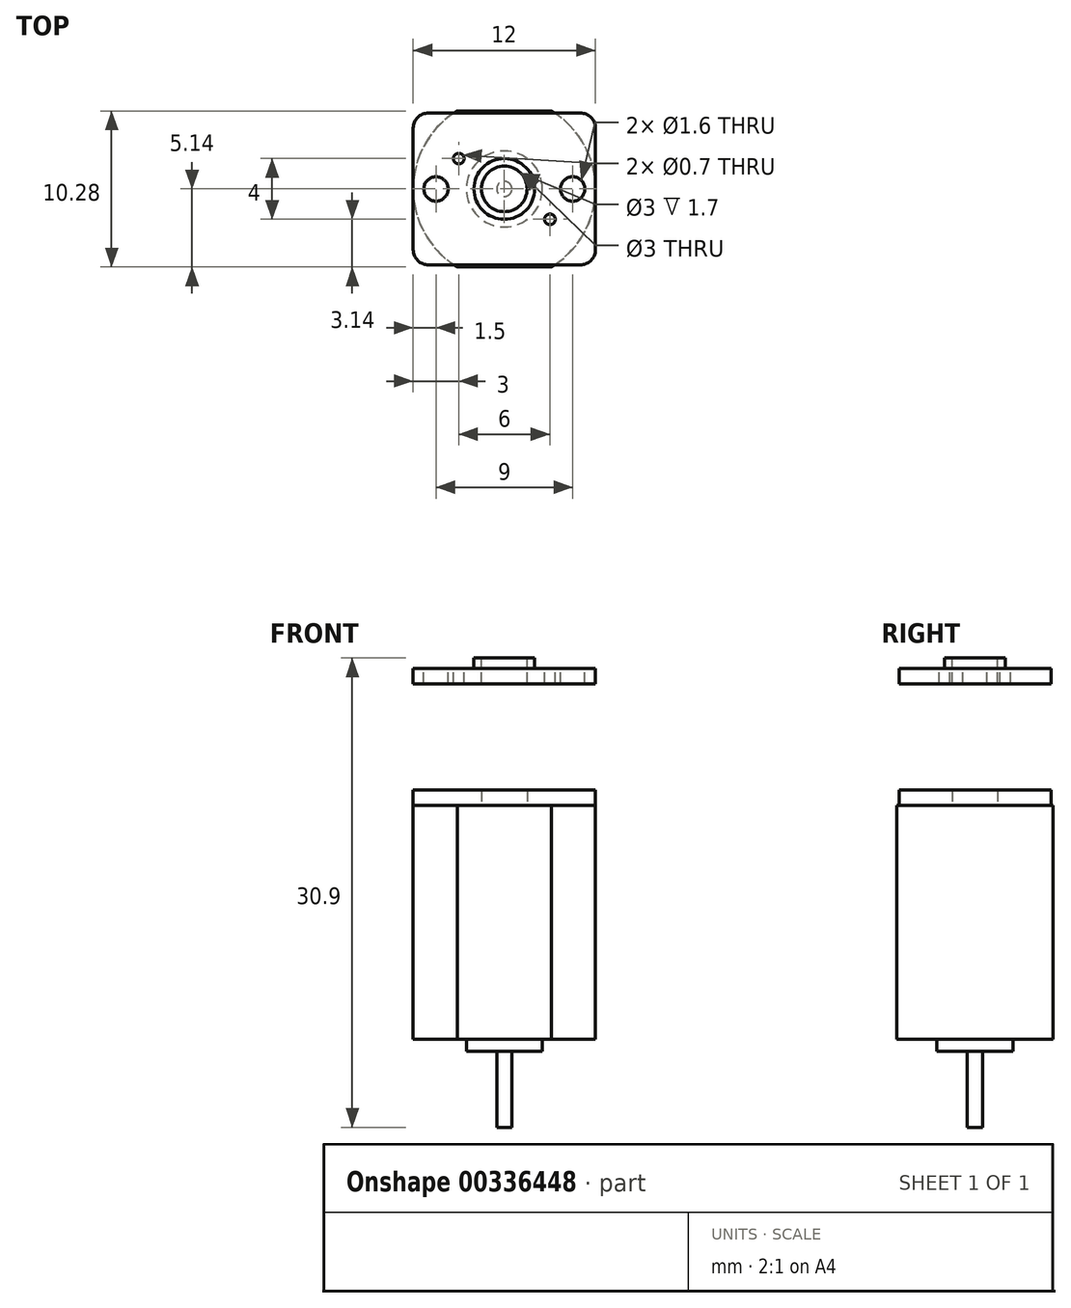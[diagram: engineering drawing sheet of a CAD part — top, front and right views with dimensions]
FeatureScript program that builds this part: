
annotation { "Feature Type Name" : "Feature", "Feature Type Description" : "" }
export const myFeature = defineFeature(function(context is Context, id is Id, definition is map)
    precondition{}
    {
        {
            var Q0;
            Q0=qCreatedBy(makeId("Top.planeOp"),FACE);
            var sketch = newSketch(context, id + "F0", { "sketchPlane" : qUnion([Q0])});
            skArc(sketch, "E0", {"start": v(-3.1, 5.14) * mm, "mid": v(-6, 0) * mm, "end": v(-3.1, -5.14) * mm});
            skLineSegment(sketch, "E1.bottom", {"start": v(-3.1, 5.14) * mm, "end": v(3.1, 5.14) * mm});
            skLineSegment(sketch, "E1.top", {"start": v(-3.1, -5.14) * mm, "end": v(3.1, -5.14) * mm});
            skArc(sketch, "E2.trimOffspring", {"start": v(3.1, -5.14) * mm, "mid": v(6, 0) * mm, "end": v(3.1, 5.14) * mm});
            skSolve(sketch);
        }
        {
            var Q0;
            Q0=makeQuery(id+"F0.imprint","IMPRINT",FACE,{"disambiguationData":[TD([[makeQuery(id+"F0.imprint","IMPRINT",EDGE,{"derivedFrom":sQuery(id+"F0.wireOp",EDGE,"E0")}),1.0]])]});
            extrude(context, id + "F1", {"entities" : qUnion([Q0]), "oppositeDirection" : true, "depth" : 15.4 * mm});
        }
        {
            var Q0;
            Q0=makeQuery(id+"F1.opExtrude","CAP_FACE",FACE,{"disambiguationData":[OSD([sQuery(id+"F0.wireOp",EDGE,"E0"),sQuery(id+"F0.wireOp",EDGE,"E1.bottom"),sQuery(id+"F0.wireOp",EDGE,"E1.top"),sQuery(id+"F0.wireOp",EDGE,"E2.trimOffspring")])],"isStart":false});
            var sketch = newSketch(context, id + "F2", { "sketchPlane" : qUnion([Q0])});
            skCircle(sketch, "E3", {"center": v(0, 0) * mm, "radius": 2.5 * mm});
            skSolve(sketch);
        }
        {
            var Q0;
            Q0=makeQuery(id+"F2.imprint","IMPRINT",FACE,{"disambiguationData":[TD([[makeQuery(id+"F2.imprint","IMPRINT",EDGE,{"derivedFrom":sQuery(id+"F2.wireOp",EDGE,"E3")}),1.0]])]});
            extrude(context, id + "F3", {"entities" : qUnion([Q0]), "operationType" : NewBodyOperationType.ADD, "depth" : .8 * mm});
        }
        {
            var Q0;
            Q0=makeQuery(id+"F3.opExtrude","CAP_FACE",FACE,{"disambiguationData":[OSD([sQuery(id+"F2.wireOp",EDGE,"E3")])],"isStart":false});
            var sketch = newSketch(context, id + "F4", { "sketchPlane" : qUnion([Q0])});
            skCircle(sketch, "E4", {"center": v(0, 0) * mm, "radius": 0.5 * mm});
            skSolve(sketch);
        }
        {
            var Q0;
            Q0=makeQuery(id+"F4.imprint","IMPRINT",FACE,{"disambiguationData":[TD([[makeQuery(id+"F4.imprint","IMPRINT",EDGE,{"derivedFrom":sQuery(id+"F4.wireOp",EDGE,"E4")}),1.0]])]});
            extrude(context, id + "F5", {"entities" : qUnion([Q0]), "operationType" : NewBodyOperationType.ADD, "depth" : 5 * mm});
        }
        {
            var Q0;
            Q0=makeQuery(id+"F1.opExtrude","CAP_FACE",FACE,{"disambiguationData":[OSD([sQuery(id+"F0.wireOp",EDGE,"E0"),sQuery(id+"F0.wireOp",EDGE,"E1.bottom"),sQuery(id+"F0.wireOp",EDGE,"E1.top"),sQuery(id+"F0.wireOp",EDGE,"E2.trimOffspring")])],"isStart":true});
            var sketch = newSketch(context, id + "F6", { "sketchPlane" : qUnion([Q0])});
            skLineSegment(sketch, "E5.bottom", {"start": v(-5, -5) * mm, "end": v(5, -5) * mm});
            skLineSegment(sketch, "E5.top", {"start": v(-5, 5) * mm, "end": v(5, 5) * mm});
            skLineSegment(sketch, "E5.left", {"start": v(-6, -4) * mm, "end": v(-6, 4) * mm});
            skLineSegment(sketch, "E5.right", {"start": v(6, -4) * mm, "end": v(6, 4) * mm});
            skPoint(sketch, "E5.middle", {"position": v(0, 0) * mm});
            skPoint(sketch, "E6.visualSharp", {"position": v(6, 5) * mm});
            skArc(sketch, "E6.filletArc", {"start": v(6, 4) * mm, "mid": v(5.7, 4.7) * mm, "end": v(5, 5) * mm});
            skPoint(sketch, "E7.visualSharp", {"position": v(6, -5) * mm});
            skArc(sketch, "E7.filletArc", {"start": v(5, -5) * mm, "mid": v(5.7, -4.7) * mm, "end": v(6, -4) * mm});
            skPoint(sketch, "E8.visualSharp", {"position": v(-6, -5) * mm});
            skArc(sketch, "E8.filletArc", {"start": v(-6, -4) * mm, "mid": v(-5.7, -4.7) * mm, "end": v(-5, -5) * mm});
            skPoint(sketch, "E9.visualSharp", {"position": v(-6, 5) * mm});
            skArc(sketch, "E9.filletArc", {"start": v(-5, 5) * mm, "mid": v(-5.7, 4.7) * mm, "end": v(-6, 4) * mm});
            skCircle(sketch, "E10", {"center": v(0, 0) * mm, "radius": 1.5 * mm});
            skSolve(sketch);
        }
        {
            var Q0;
            Q0 = qSketchRegion(id + "F6", true);
            extrude(context, id + "F7", {"entities" : qUnion([Q0]), "depth" : 1 * mm});
        }
        {
            var Q0;
            Q0=makeQuery(id+"F1.opExtrude","CAP_FACE",FACE,{"disambiguationData":[OSD([sQuery(id+"F0.wireOp",EDGE,"E0"),sQuery(id+"F0.wireOp",EDGE,"E1.bottom"),sQuery(id+"F0.wireOp",EDGE,"E1.top"),sQuery(id+"F0.wireOp",EDGE,"E2.trimOffspring")])],"isStart":true});
            cPlane(context, id + "F8", {"entities" : qUnion([Q0]), "cplaneType" : CPlaneType.OFFSET, "offset" : 9 * mm, "width" : 150 * mm, "height" : 150 * mm});
        }
        {
            var Q0;
            Q0=qCreatedBy(id+"F8.planeOp",FACE);
            var sketch = newSketch(context, id + "F9", { "sketchPlane" : qUnion([Q0])});
            skLineSegment(sketch, "E11.0", {"start": v(-5, -5) * mm, "end": v(5, -5) * mm});
            skArc(sketch, "E12.0", {"start": v(5, -5) * mm, "mid": v(5.7, -4.7) * mm, "end": v(6, -4) * mm});
            skLineSegment(sketch, "E13.0", {"start": v(6, -4) * mm, "end": v(6, 4) * mm});
            skLineSegment(sketch, "E14.0", {"start": v(-6, -4) * mm, "end": v(-6, 4) * mm});
            skArc(sketch, "E15.0", {"start": v(-6, -4) * mm, "mid": v(-5.7, -4.7) * mm, "end": v(-5, -5) * mm});
            skArc(sketch, "E16.0", {"start": v(-5, 5) * mm, "mid": v(-5.7, 4.7) * mm, "end": v(-6, 4) * mm});
            skLineSegment(sketch, "E17.0", {"start": v(-5, 5) * mm, "end": v(5, 5) * mm});
            skArc(sketch, "E18.0", {"start": v(6, 4) * mm, "mid": v(5.7, 4.7) * mm, "end": v(5, 5) * mm});
            skCircle(sketch, "E19.0", {"center": v(0, 0) * mm, "radius": 1.5 * mm});
            skCircle(sketch, "E20", {"center": v(-4.5, 0) * mm, "radius": 0.8 * mm});
            skCircle(sketch, "E21.MirrorC", {"center": v(4.5, 0) * mm, "radius": 0.8 * mm});
            skCircle(sketch, "E22", {"center": v(3, -2) * mm, "radius": 0.35 * mm});
            skLineSegment(sketch, "E23", {"start": v(3, -2) * mm, "end": v(0, 0) * mm, "construction": true});
            skLineSegment(sketch, "E24", {"start": v(0, 0) * mm, "end": v(-3, 2) * mm, "construction": true});
            skCircle(sketch, "E25", {"center": v(-3, 2) * mm, "radius": 0.35 * mm});
            skSolve(sketch);
        }
        {
            var Q0;
            Q0=makeQuery(id+"F9.imprint","IMPRINT",FACE,{"disambiguationData":[TD([[makeQuery(id+"F9.imprint","IMPRINT",EDGE,{"derivedFrom":sQuery(id+"F9.wireOp",EDGE,"E11.0")}),1.0]])]});
            extrude(context, id + "F10", {"entities" : qUnion([Q0]), "oppositeDirection" : true, "depth" : 1 * mm});
        }
        {
            var Q0;
            Q0=makeQuery(id+"F10.opExtrude","CAP_FACE",FACE,{"disambiguationData":[OSD([sQuery(id+"F9.wireOp",EDGE,"E11.0"),sQuery(id+"F9.wireOp",EDGE,"E12.0"),sQuery(id+"F9.wireOp",EDGE,"E13.0"),sQuery(id+"F9.wireOp",EDGE,"E14.0"),sQuery(id+"F9.wireOp",EDGE,"E15.0"),sQuery(id+"F9.wireOp",EDGE,"E16.0"),sQuery(id+"F9.wireOp",EDGE,"E17.0"),sQuery(id+"F9.wireOp",EDGE,"E18.0"),sQuery(id+"F9.wireOp",EDGE,"E19.0"),sQuery(id+"F9.wireOp",EDGE,"E20"),sQuery(id+"F9.wireOp",EDGE,"E21.MirrorC"),sQuery(id+"F9.wireOp",EDGE,"E22"),sQuery(id+"F9.wireOp",EDGE,"E25")])],"isStart":true});
            var sketch = newSketch(context, id + "F11", { "sketchPlane" : qUnion([Q0])});
            skCircle(sketch, "E26", {"center": v(0, 0) * mm, "radius": 2 * mm});
            skCircle(sketch, "E27.0", {"center": v(0, 0) * mm, "radius": 1.5 * mm});
            skSolve(sketch);
        }
        {
            var Q0;
            Q0=makeQuery(id+"F11.imprint","IMPRINT",FACE,{"disambiguationData":[TD([[makeQuery(id+"F11.imprint","IMPRINT",EDGE,{"derivedFrom":sQuery(id+"F11.wireOp",EDGE,"E26")}),1.0]])]});
            extrude(context, id + "F12", {"entities" : qUnion([Q0]), "operationType" : NewBodyOperationType.ADD, "depth" : .7 * mm});
        }
    });
